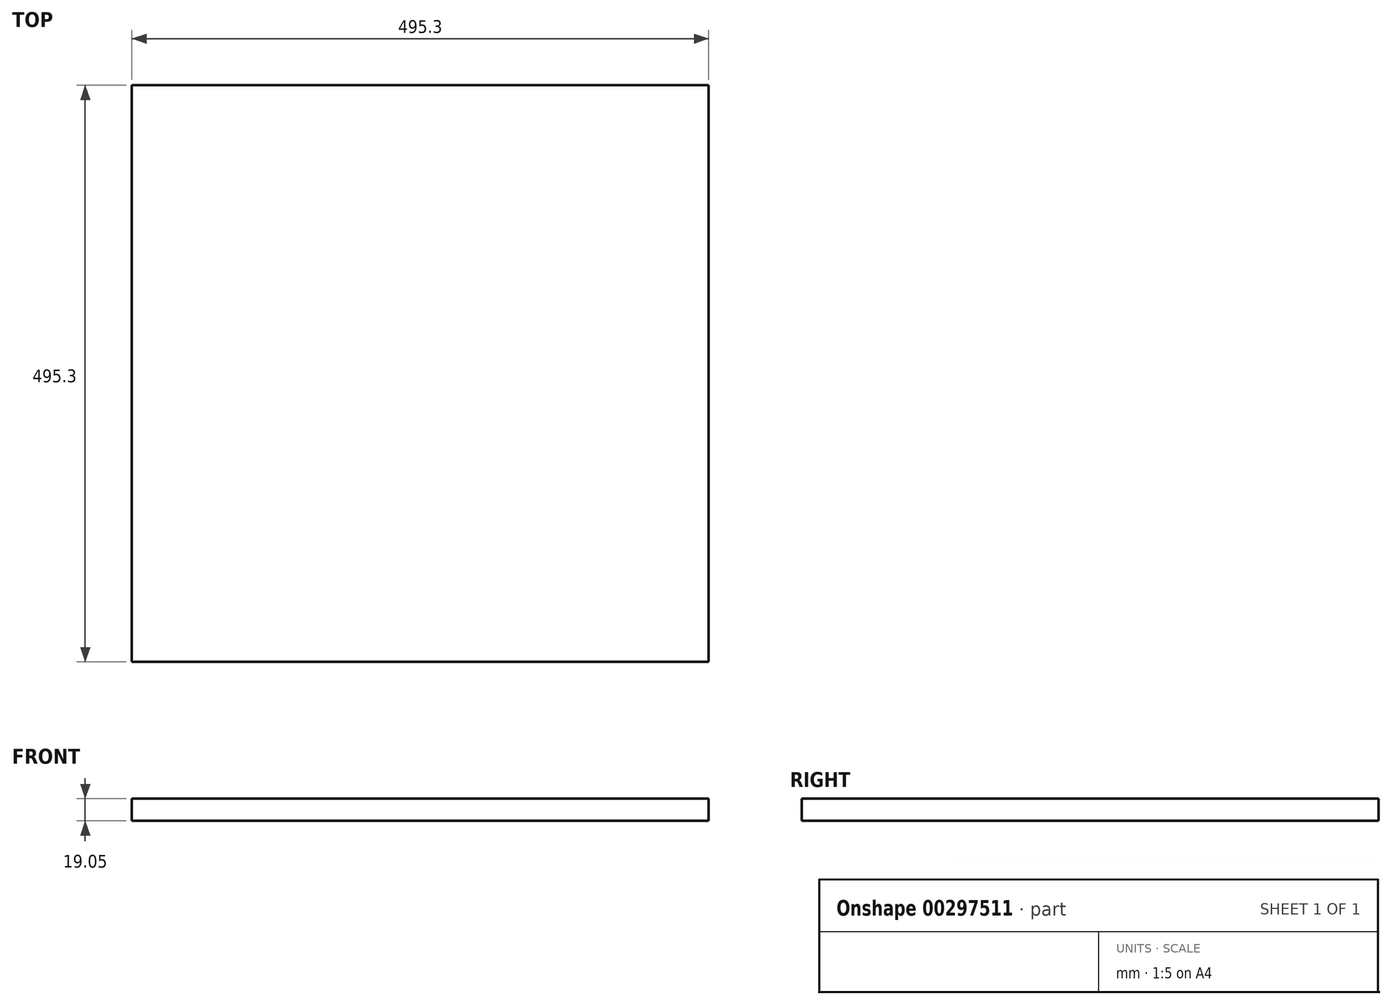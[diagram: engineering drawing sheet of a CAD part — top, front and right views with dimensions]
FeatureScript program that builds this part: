
annotation { "Feature Type Name" : "Feature", "Feature Type Description" : "" }
export const myFeature = defineFeature(function(context is Context, id is Id, definition is map)
    precondition{}
    {
        {
            var Q0;
            Q0=qCreatedBy(makeId("Top.planeOp"),FACE);
            var sketch = newSketch(context, id + "F0", { "sketchPlane" : qUnion([Q0])});
            skLineSegment(sketch, "E0.bottom", {"start": v(0, 0) * mm, "end": v(495.3, 0) * mm});
            skLineSegment(sketch, "E0.left", {"start": v(0, 0) * mm, "end": v(0, 495.3) * mm});
            skLineSegment(sketch, "E0.right", {"start": v(495.3, 0) * mm, "end": v(495.3, 495.3) * mm});
            skLineSegment(sketch, "E1", {"start": v(0, 495.3) * mm, "end": v(495.3, 495.3) * mm});
            skSolve(sketch);
        }
        {
            var Q0;
            Q0=makeQuery(id+"F0.imprint","IMPRINT",FACE,{"disambiguationData":[TD([[makeQuery(id+"F0.imprint","IMPRINT",EDGE,{"derivedFrom":sQuery(id+"F0.wireOp",EDGE,"E0.bottom")}),1.0]])]});
            extrude(context, id + "F1", {"entities" : qUnion([Q0]), "depth" : 19.05 * mm});
        }
    });
